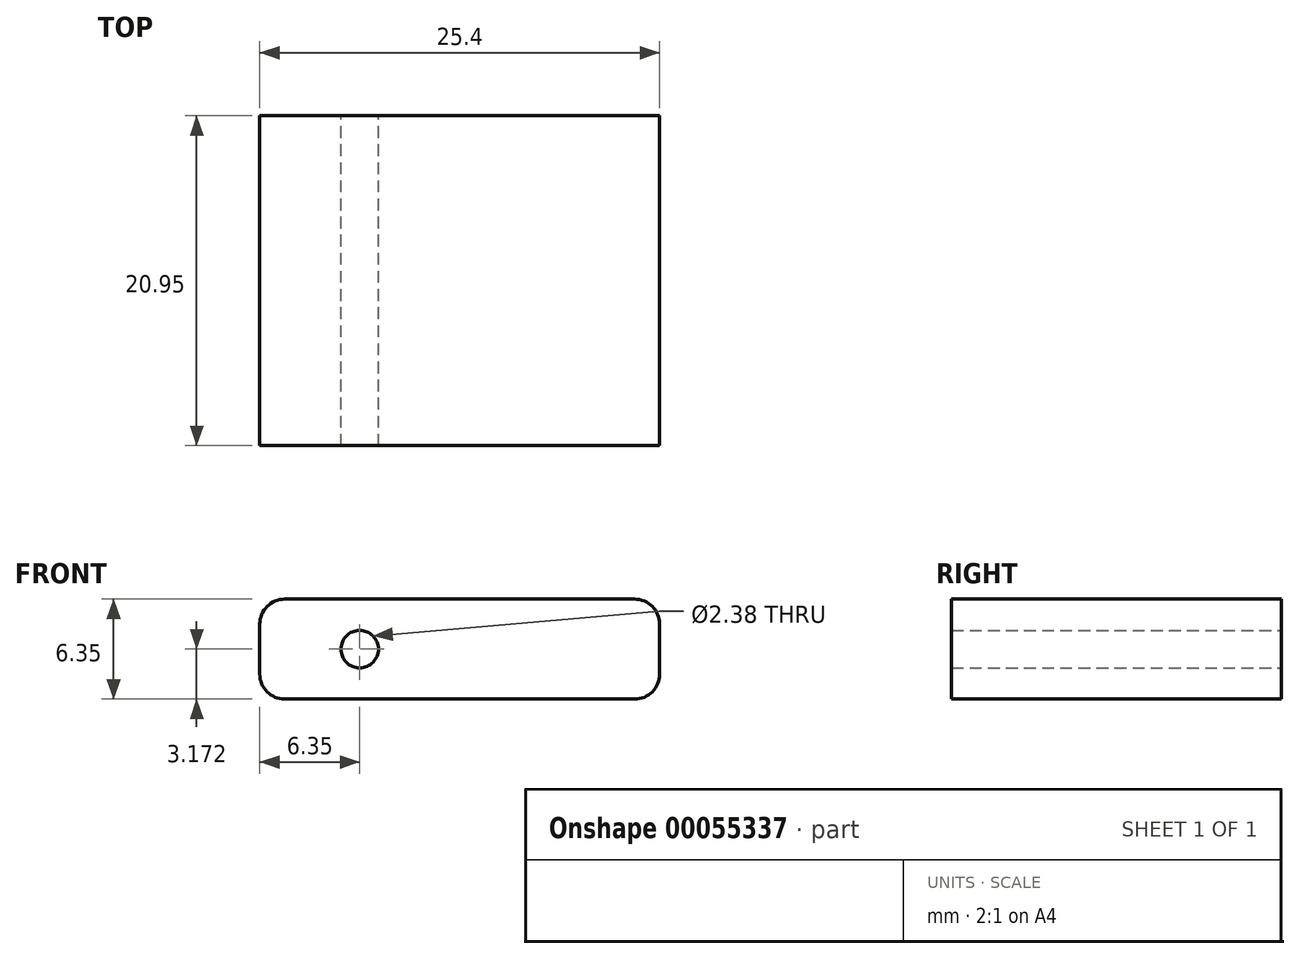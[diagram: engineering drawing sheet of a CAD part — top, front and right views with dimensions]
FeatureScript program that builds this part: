
annotation { "Feature Type Name" : "Feature", "Feature Type Description" : "" }
export const myFeature = defineFeature(function(context is Context, id is Id, definition is map)
    precondition{}
    {
        {
            var Q0;
            Q0=qCreatedBy(makeId("Right.planeOp"),FACE);
            var sketch = newSketch(context, id + "F0", { "sketchPlane" : qUnion([Q0])});
            skLineSegment(sketch, "E0.bottom", {"start": v(-23.7, 25.16) * mm, "end": v(-2.75, 25.16) * mm});
            skLineSegment(sketch, "E0.top", {"start": v(-23.7, 18.8) * mm, "end": v(-2.75, 18.8) * mm});
            skLineSegment(sketch, "E0.left", {"start": v(-23.7, 25.16) * mm, "end": v(-23.7, 18.8) * mm});
            skLineSegment(sketch, "E0.right", {"start": v(-2.75, 25.16) * mm, "end": v(-2.75, 18.8) * mm});
            skSolve(sketch);
        }
        {
            var Q0;
            Q0=makeQuery(id+"F0.imprint","IMPRINT",FACE,{"disambiguationData":[TD([[makeQuery(id+"F0.imprint","IMPRINT",EDGE,{"derivedFrom":sQuery(id+"F0.wireOp",EDGE,"E0.bottom")}),-1.0]])]});
            extrude(context, id + "F1", {"entities" : qUnion([Q0]), "depth" : 25.4 * mm});
        }
        {
            var Q0;
            Q0=makeQuery(id+"F1.opExtrude","CAP_EDGE",EDGE,{"disambiguationData":[OSD([sQuery(id+"F0.wireOp",EDGE,"E0.bottom")])],"isStart":false});
            var Q1;
            Q1=makeQuery(id+"F1.opExtrude","CAP_EDGE",EDGE,{"disambiguationData":[OSD([sQuery(id+"F0.wireOp",EDGE,"E0.top")])],"isStart":false});
            var Q2;
            Q2=makeQuery(id+"F1.opExtrude","CAP_EDGE",EDGE,{"disambiguationData":[OSD([sQuery(id+"F0.wireOp",EDGE,"E0.top")])],"isStart":true});
            var Q3;
            Q3=makeQuery(id+"F1.opExtrude","CAP_EDGE",EDGE,{"disambiguationData":[OSD([sQuery(id+"F0.wireOp",EDGE,"E0.bottom")])],"isStart":true});
            fillet(context, id + "F2", {"entities" : qUnion([Q0, Q1, Q2, Q3]), "radius" : 1.59 * mm, "tangentPropagation" : true, "allowEdgeOverflow" : false});
        }
        {
            var Q0;
            Q0=makeQuery(id+"F1.opExtrude","SWEPT_FACE",FACE,{"disambiguationData":[OSD([sQuery(id+"F0.wireOp",EDGE,"E0.right")])]});
            var sketch = newSketch(context, id + "F3", { "sketchPlane" : qUnion([Q0])});
            skCircle(sketch, "E1", {"center": v(-6.35, 21.98) * mm, "radius": 1.2 * mm});
            skSolve(sketch);
        }
        {
            var Q0;
            Q0=makeQuery(id+"F3.imprint","IMPRINT",FACE,{"disambiguationData":[TD([[makeQuery(id+"F3.imprint","IMPRINT",EDGE,{"derivedFrom":sQuery(id+"F3.wireOp",EDGE,"E1")}),1.0]])]});
            extrude(context, id + "F4", {"entities" : qUnion([Q0]), "operationType" : NewBodyOperationType.REMOVE, "oppositeDirection" : true, "depth" : 25.4 * mm});
        }
    });
